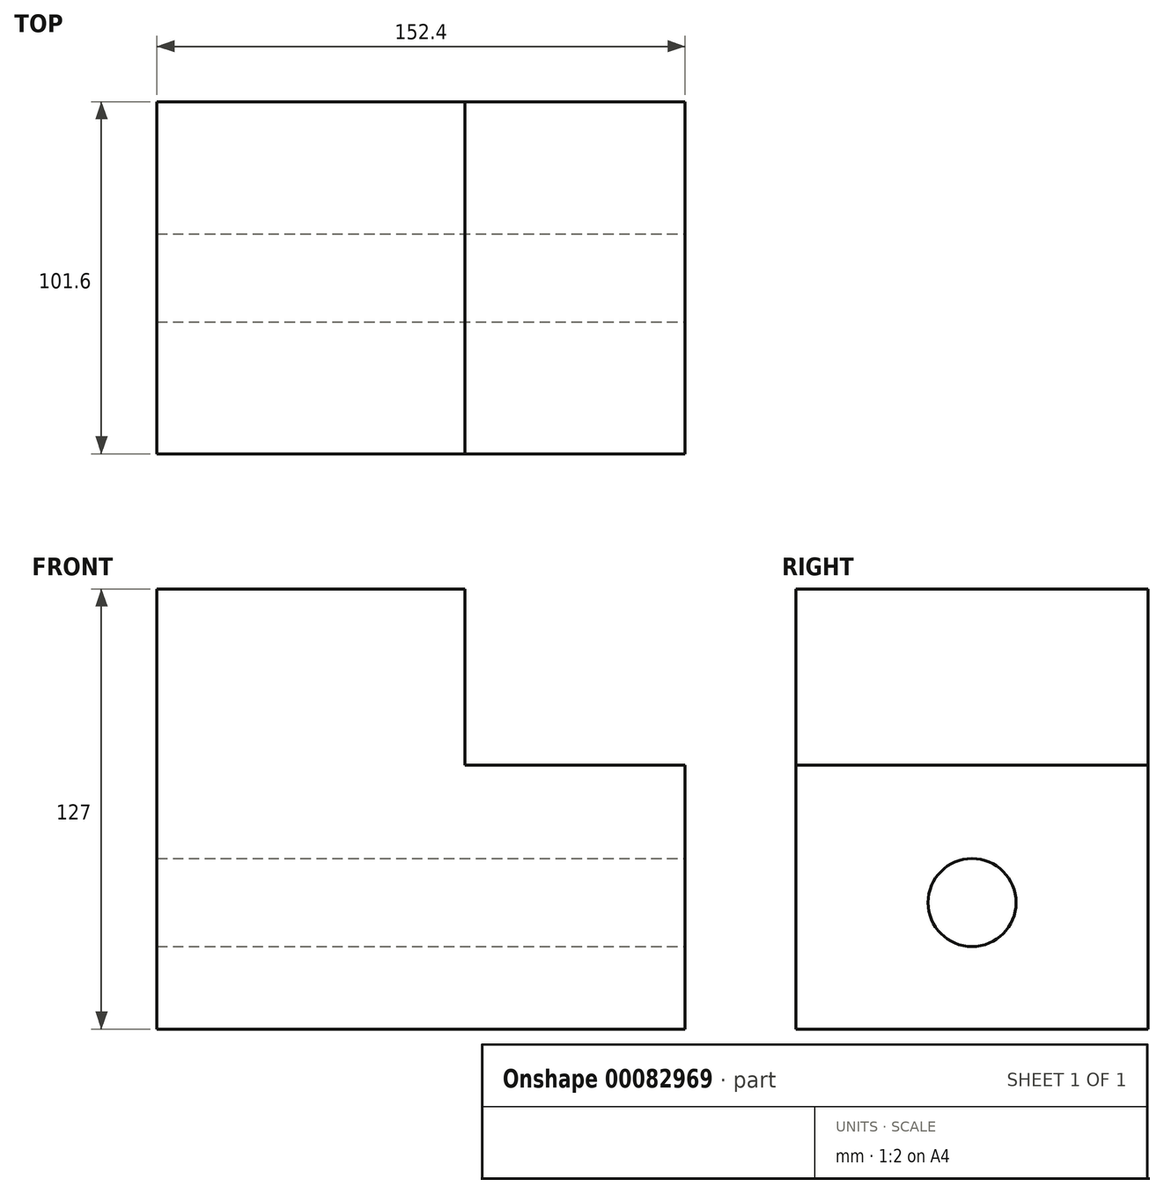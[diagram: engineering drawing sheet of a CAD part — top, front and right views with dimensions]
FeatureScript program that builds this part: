
annotation { "Feature Type Name" : "Feature", "Feature Type Description" : "" }
export const myFeature = defineFeature(function(context is Context, id is Id, definition is map)
    precondition{}
    {
        {
            var Q0;
            Q0=qCreatedBy(makeId("Top.planeOp"),FACE);
            var sketch = newSketch(context, id + "F0", { "sketchPlane" : qUnion([Q0])});
            skLineSegment(sketch, "E0.bottom", {"start": v(-53.72, 25.26) * mm, "end": v(98.68, 25.26) * mm});
            skLineSegment(sketch, "E0.top", {"start": v(-53.72, -76.34) * mm, "end": v(98.68, -76.34) * mm});
            skLineSegment(sketch, "E0.left", {"start": v(-53.72, 25.26) * mm, "end": v(-53.72, -76.34) * mm});
            skLineSegment(sketch, "E0.right", {"start": v(98.68, 25.26) * mm, "end": v(98.68, -76.34) * mm});
            skSolve(sketch);
        }
        {
            var Q0;
            Q0=makeQuery(id+"F0.imprint","IMPRINT",FACE,{"disambiguationData":[TD([[makeQuery(id+"F0.imprint","IMPRINT",EDGE,{"derivedFrom":sQuery(id+"F0.wireOp",EDGE,"E0.bottom")}),-1.0]])]});
            extrude(context, id + "F1", {"entities" : qUnion([Q0]), "depth" : 127 * mm});
        }
        {
            var Q0;
            Q0=makeQuery(id+"F1.opExtrude","SWEPT_FACE",FACE,{"disambiguationData":[OSD([sQuery(id+"F0.wireOp",EDGE,"E0.right")])]});
            var sketch = newSketch(context, id + "F2", { "sketchPlane" : qUnion([Q0])});
            skLineSegment(sketch, "E1.bottom", {"start": v(-76.34, 127) * mm, "end": v(25.26, 127) * mm});
            skLineSegment(sketch, "E1.top", {"start": v(-76.34, 76.2) * mm, "end": v(25.26, 76.2) * mm});
            skLineSegment(sketch, "E1.left", {"start": v(-76.34, 127) * mm, "end": v(-76.34, 76.2) * mm});
            skLineSegment(sketch, "E1.right", {"start": v(25.26, 127) * mm, "end": v(25.26, 76.2) * mm});
            skSolve(sketch);
        }
        {
            var Q0;
            Q0=makeQuery(id+"F2.imprint","IMPRINT",FACE,{"disambiguationData":[TD([[makeQuery(id+"F2.imprint","IMPRINT",EDGE,{"derivedFrom":sQuery(id+"F2.wireOp",EDGE,"E1.bottom")}),1.0]])]});
            extrude(context, id + "F3", {"entities" : qUnion([Q0]), "operationType" : NewBodyOperationType.REMOVE, "oppositeDirection" : true, "depth" : 63.5 * mm});
        }
        {
            var Q0;
            Q0=makeQuery(id+"F1.opExtrude","SWEPT_FACE",FACE,{"disambiguationData":[OSD([sQuery(id+"F0.wireOp",EDGE,"E0.right")])]});
            var sketch = newSketch(context, id + "F4", { "sketchPlane" : qUnion([Q0])});
            skCircle(sketch, "E2", {"center": v(-25.54, 36.49) * mm, "radius": 12.7 * mm});
            skPoint(sketch, "E2.centerSnap0", {"position": v(-25.54, 0) * mm});
            skSolve(sketch);
        }
        {
            var Q0;
            Q0=sQuery(id+"F4.wireOp",VERTEX,"E2.center");
            var Q1;
            Q1=makeQuery(id+"F1.opExtrude","SWEPT_BODY",BODY,{"disambiguationData":[OSD([sQuery(id+"F0.wireOp",EDGE,"E0.bottom"),sQuery(id+"F0.wireOp",EDGE,"E0.top"),sQuery(id+"F0.wireOp",EDGE,"E0.left"),sQuery(id+"F0.wireOp",EDGE,"E0.right")])]});
            hole(context, id + "F5", {"style" : HoleStyle.SIMPLE, "endStyle" : HoleEndStyle.THROUGH, "holeDiameter" : 25.4 * mm, "locations" : qUnion([Q0]), "scope" : qUnion([Q1]), "isTappedThrough" : true});
        }
    });
